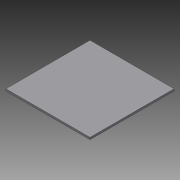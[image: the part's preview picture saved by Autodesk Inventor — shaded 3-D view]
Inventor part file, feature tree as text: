
AUTODESK INVENTOR PART (.ipt)
format: ipt  version: 2015 (Build 190159000, 159)  size: 67,584 bytes
history: native  units: mm
features: other x1, extrude x1, sketch x1
ambient origin geometry x8: Origin, YZ Plane, XZ Plane, XY Plane, X Axis, Y Axis, Z Axis, Center Point
bodies: Body1 (feature_tree)
feature tree (3):
  other  "ソリッド1"
  extrude  "押し出し1"  Depth=40.0mm
  sketch  "スケッチ1"
